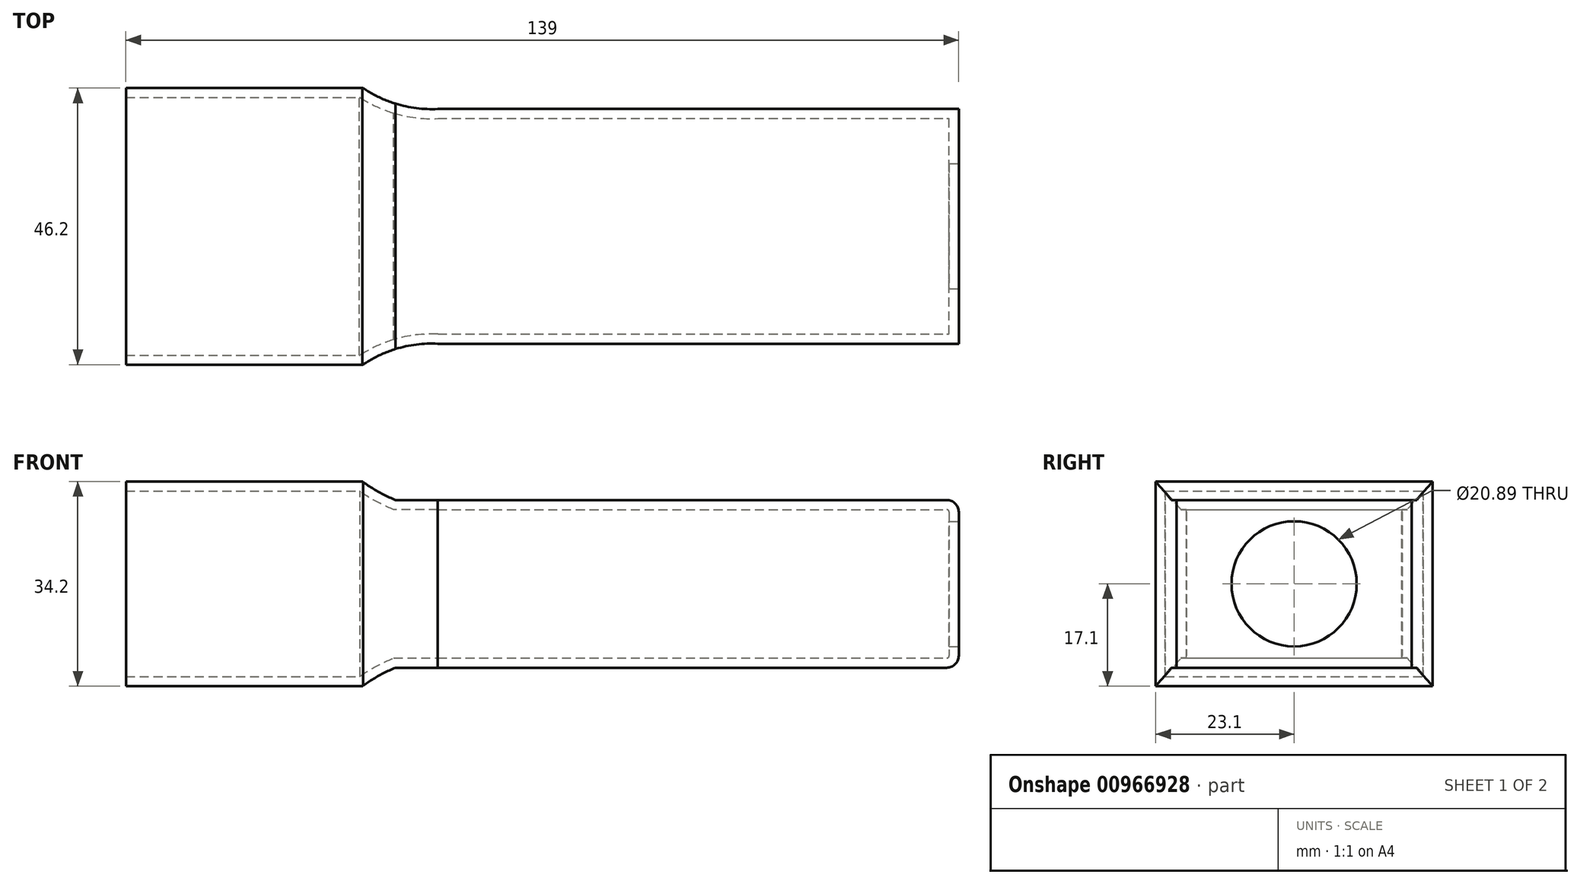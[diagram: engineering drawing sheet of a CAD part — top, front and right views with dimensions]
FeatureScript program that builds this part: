
annotation { "Feature Type Name" : "Feature", "Feature Type Description" : "" }
export const myFeature = defineFeature(function(context is Context, id is Id, definition is map)
    precondition{}
    {
        {
            var Q0;
            Q0=qCreatedBy(makeId("Front.planeOp"),FACE);
            var sketch = newSketch(context, id + "F0", { "sketchPlane" : qUnion([Q0])});
            skLineSegment(sketch, "E0.bottom", {"start": v(-46.5, 14) * mm, "end": v(45.5, 14) * mm});
            skLineSegment(sketch, "E0.top", {"start": v(-46.5, -14) * mm, "end": v(45.5, -14) * mm});
            skLineSegment(sketch, "E0.right", {"start": v(47.5, 12) * mm, "end": v(47.5, -12) * mm});
            skPoint(sketch, "E0.middle", {"position": v(0, 0) * mm});
            skLineSegment(sketch, "E1.bottom", {"start": v(-91.5, 17.1) * mm, "end": v(-52.02, 17.1) * mm});
            skLineSegment(sketch, "E1.top", {"start": v(-91.5, -17.1) * mm, "end": v(-49.5, -17.1) * mm});
            skLineSegment(sketch, "E1.left", {"start": v(-91.5, 17.1) * mm, "end": v(-91.5, -17.1) * mm});
            skLineSegment(sketch, "E2", {"start": v(-91.5, 17.1) * mm, "end": v(-47.5, -17.1) * mm, "construction": true});
            skPoint(sketch, "E3", {"position": v(-69.5, 0) * mm});
            skPoint(sketch, "E4", {"position": v(-47.5, 0) * mm});
            skPoint(sketch, "E5.visualSharp", {"position": v(-47.5, 17.1) * mm});
            skPoint(sketch, "E6.visualSharp", {"position": v(-47.5, -17.1) * mm});
            skPoint(sketch, "E7.visualSharp", {"position": v(47.5, 14) * mm});
            skArc(sketch, "E7.filletArc", {"start": v(47.5, 12) * mm, "mid": v(46.92, 13.41) * mm, "end": v(45.5, 14) * mm});
            skPoint(sketch, "E8.visualSharp", {"position": v(47.5, -14) * mm});
            skArc(sketch, "E8.filletArc", {"start": v(45.5, -14) * mm, "mid": v(46.92, -13.41) * mm, "end": v(47.5, -12) * mm});
            skArc(sketch, "E9", {"start": v(-52.02, 17.1) * mm, "mid": v(-49.35, 15.38) * mm, "end": v(-46.5, 14) * mm});
            skArc(sketch, "E10.MirrorCS", {"start": v(-52.02, -17.1) * mm, "mid": v(-49.35, -15.38) * mm, "end": v(-46.5, -14) * mm});
            skPoint(sketch, "E0.left.start.orphan", {"position": v(-47.5, 14) * mm});
            skPoint(sketch, "E11.orphan", {"position": v(-47.5, -14) * mm});
            skLineSegment(sketch, "E12", {"start": v(-91.5, 0) * mm, "end": v(47.5, 0) * mm, "construction": true});
            skSolve(sketch);
        }
        {
            var Q0;
            Q0=makeQuery(id+"F0.imprint","IMPRINT",FACE,{"disambiguationData":[TD([[makeQuery(id+"F0.imprint","IMPRINT",EDGE,{"derivedFrom":sQuery(id+"F0.wireOp",EDGE,"E0.bottom")}),-1.0]])]});
            extrude(context, id + "F1", {"entities" : qUnion([Q0]), "depth" : (43 + 1.6 + 1.6) * mm, "offsetDistance" : 25 * mm});
        }
        {
            var Q0;
            Q0=makeQuery(id+"F1.opExtrude","SWEPT_FACE",FACE,{"disambiguationData":[OSD([sQuery(id+"F0.wireOp",EDGE,"E0.bottom")])]});
            var sketch = newSketch(context, id + "F2", { "sketchPlane" : qUnion([Q0])});
            skLineSegment(sketch, "E13", {"start": v(-39.45, -3.5) * mm, "end": v(66.12, -3.5) * mm});
            skLineSegment(sketch, "E14", {"start": v(-51.9, 0) * mm, "end": v(-43.36, 13.49) * mm});
            skLineSegment(sketch, "E15", {"start": v(-43.36, 13.49) * mm, "end": v(64.58, 13.49) * mm});
            skLineSegment(sketch, "E16", {"start": v(64.58, 13.49) * mm, "end": v(66.12, -3.5) * mm});
            skLineSegment(sketch, "E17", {"start": v(-46.5, -23.1) * mm, "end": v(79.26, -23.1) * mm, "construction": true});
            skLineSegment(sketch, "E18.MirrorCS", {"start": v(-39.45, -42.7) * mm, "end": v(66.12, -42.7) * mm});
            skLineSegment(sketch, "E19.MirrorCS", {"start": v(-51.9, -46.2) * mm, "end": v(-43.36, -59.69) * mm});
            skPoint(sketch, "E20.MirrorCS.end.orphan", {"position": v(-39.45, -42.7) * mm});
            skPoint(sketch, "E20.MirrorCS.start.orphan", {"position": v(-51.9, -46.2) * mm});
            skArc(sketch, "E21", {"start": v(-51.9, 0) * mm, "mid": v(-45.97, -2.78) * mm, "end": v(-39.45, -3.5) * mm});
            skArc(sketch, "E22.MirrorCS", {"start": v(-51.9, -46.2) * mm, "mid": v(-45.97, -43.42) * mm, "end": v(-39.45, -42.7) * mm});
            skLineSegment(sketch, "E23.MirrorCS", {"start": v(-43.36, -59.69) * mm, "end": v(64.58, -59.69) * mm});
            skLineSegment(sketch, "E24.MirrorCS", {"start": v(64.58, -59.69) * mm, "end": v(66.12, -42.7) * mm});
            skLineSegment(sketch, "E25", {"start": v(-31.01, -3.5) * mm, "end": v(-31.01, -42.7) * mm, "construction": true});
            skSolve(sketch);
        }
        {
            var Q0;
            {var subQ0=sQuery(id+"F0.wireOp",EDGE,"E0.bottom");var subQ1=makeQuery(id+"F1.opExtrude","CAP_EDGE",EDGE,{"disambiguationData":[OSD([subQ0])],"isStart":false});Q0=makeQuery(id+"F2.imprint","IMPRINT",FACE,{"disambiguationData":[TD([[makeQuery(id+"F2.imprint","IMPRINT",EDGE,{"derivedFrom":subQ1}),1.0]])]});}
            var Q1;
            {var subQ0=sQuery(id+"F0.wireOp",EDGE,"E0.bottom");var subQ1=makeQuery(id+"F1.opExtrude","CAP_EDGE",EDGE,{"disambiguationData":[OSD([subQ0])],"isStart":true});Q1=makeQuery(id+"F2.imprint","IMPRINT",FACE,{"disambiguationData":[TD([[makeQuery(id+"F2.imprint","IMPRINT",EDGE,{"derivedFrom":subQ1}),-1.0]])]});}
            var Q2;
            {var subQ1=sQuery(id+"F2.wireOp",EDGE,"E19.MirrorCS");Q2=makeQuery(id+"F2.imprint","IMPRINT",FACE,{"disambiguationData":[TD([[makeQuery(id+"F2.imprint","IMPRINT",EDGE,{"derivedFrom":subQ1}),1.0]])]});}
            var Q3;
            {var subQ3=sQuery(id+"F2.wireOp",EDGE,"E14");Q3=makeQuery(id+"F2.imprint","IMPRINT",FACE,{"disambiguationData":[TD([[makeQuery(id+"F2.imprint","IMPRINT",EDGE,{"derivedFrom":subQ3}),-1.0]])]});}
            extrude(context, id + "F3", {"entities" : qUnion([Q0, Q1, Q2, Q3]), "operationType" : NewBodyOperationType.REMOVE, "endBound" : BoundingType.THROUGH_ALL, "oppositeDirection" : true, "depth" : 25 * mm, "offsetDistance" : 25 * mm, "hasSecondDirection" : true, "secondDirectionOppositeDirection" : false, "secondDirectionDepth" : 5 * mm});
        }
        {
            var Q0;
            Q0=makeQuery(id+"F1.opExtrude","SWEPT_FACE",FACE,{"disambiguationData":[OSD([sQuery(id+"F0.wireOp",EDGE,"E1.left")])]});
            shell(context, id + "F4", {"entities" : qUnion([Q0]), "thickness" : 1.6 * mm});
        }
        {
            var Q0;
            Q0=makeQuery(id+"F1.opExtrude","SWEPT_FACE",FACE,{"disambiguationData":[OSD([sQuery(id+"F0.wireOp",EDGE,"E0.right")])]});
            var sketch = newSketch(context, id + "F5", { "sketchPlane" : qUnion([Q0])});
            skCircle(sketch, "E26", {"center": v(-23.1, 0) * mm, "radius": 10.45 * mm});
            skPoint(sketch, "E26.centerSnap0", {"position": v(-23.1, 12) * mm});
            skSolve(sketch);
        }
        {
            var Q0;
            Q0=makeQuery(id+"F5.imprint","IMPRINT",FACE,{"disambiguationData":[TD([[makeQuery(id+"F5.imprint","IMPRINT",EDGE,{"derivedFrom":sQuery(id+"F5.wireOp",EDGE,"E26")}),1.0]])]});
            extrude(context, id + "F6", {"entities" : qUnion([Q0]), "operationType" : NewBodyOperationType.REMOVE, "endBound" : BoundingType.THROUGH_ALL, "oppositeDirection" : true, "depth" : 25 * mm, "offsetDistance" : 25 * mm});
        }
    });
